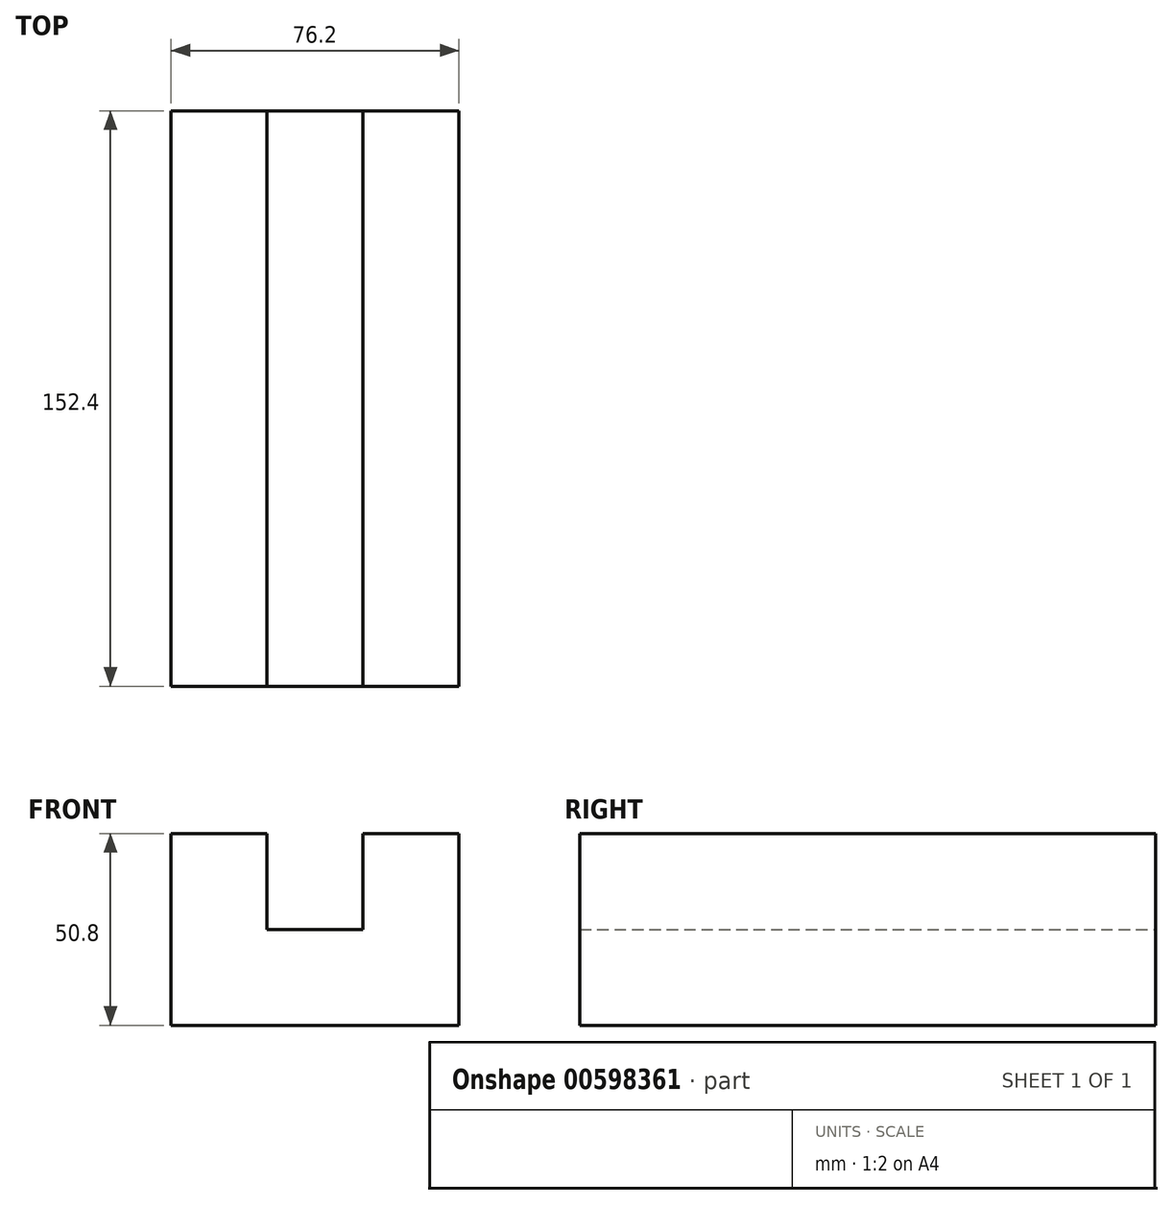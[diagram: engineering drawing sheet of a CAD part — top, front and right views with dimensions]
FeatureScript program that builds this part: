
annotation { "Feature Type Name" : "Feature", "Feature Type Description" : "" }
export const myFeature = defineFeature(function(context is Context, id is Id, definition is map)
    precondition{}
    {
        {
            var Q0;
            Q0=qCreatedBy(makeId("Front.planeOp"),FACE);
            var sketch = newSketch(context, id + "F0", { "sketchPlane" : qUnion([Q0])});
            skLineSegment(sketch, "E0", {"start": v(0, 0) * mm, "end": v(76.2, 0) * mm});
            skLineSegment(sketch, "E1", {"start": v(76.2, 0) * mm, "end": v(76.2, 50.8) * mm});
            skLineSegment(sketch, "E2", {"start": v(76.2, 50.8) * mm, "end": v(50.8, 50.8) * mm});
            skLineSegment(sketch, "E3", {"start": v(50.8, 50.8) * mm, "end": v(50.8, 25.4) * mm});
            skLineSegment(sketch, "E4", {"start": v(50.8, 25.4) * mm, "end": v(25.4, 25.4) * mm});
            skLineSegment(sketch, "E5", {"start": v(25.4, 25.4) * mm, "end": v(25.4, 50.8) * mm});
            skLineSegment(sketch, "E6", {"start": v(25.4, 50.8) * mm, "end": v(0, 50.8) * mm});
            skLineSegment(sketch, "E7", {"start": v(0, 50.8) * mm, "end": v(0, 0) * mm});
            skSolve(sketch);
        }
        {
            var Q0;
            Q0 = qSketchRegion(id + "F0", true);
            extrude(context, id + "F1", {"entities" : qUnion([Q0]), "depth" : 152.4 * mm, "offsetDistance" : 25.4 * mm});
        }
    });
